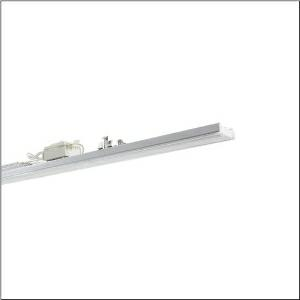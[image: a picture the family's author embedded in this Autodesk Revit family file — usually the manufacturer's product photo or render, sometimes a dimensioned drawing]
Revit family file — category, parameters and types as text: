
# Revit family: licross_21_recessed_ho_52te12dn4fxm3s
name_source: partatom
category: Lighting Fixtures
units: mm (PartAtom-declared; Revit-internal decimal feet)

## family parameters
Cut with Voids When Loaded = No
Host = Face
Light Source = No
Part Type = Normal
Room Calculation Point = No
Round Connector Dimension = Use Diameter
Shared = No

## types (1)
- --- (1 x LED, 930 lm, 7.5 W, 4000K)
    Apparent Load = 8 VA
    CIE Flux Codes = 69 91 98 100 100
    Color Rendering = 80
    Color Temperature = 4000K
    Default Elevation = 1800 mm
    Description = Licross 21 Recessed HO, luminaire insert, of sheet steel, galvanised, coil coated, white, length: 1.500mm, width: 66mm, height: 67mm, LED rated luminous flux: 15.000lm, light colour: 840, SDCM (Standard Deviation of Colour Matching)MacAdam ≤ 3 SDCM (initial), control gear: DALI 2 (for two DALI lines), with plug, 6-pole, with phase selection, for trunking rail, 14-core, mains connection: 220..240V, AC, 50/60Hz, rated input power: 88W, internal wiring halogen-free, for emergency light function, for trunking rail, 14-core, converter,control gear: single battery element, battery: LiFePO4, 9Ah, primary optical cover: cover, of PMMA, light emission: direct distribution, primary light characteristic: symmetric, protection rating (complete): IP54, insulation class (complete): insulation class I (protective earthing), certification: CE, UKCA, protection symbol: D if used in an environment with non-conductive dust loads with corresponding accessories, impact resistance: IK06, permissible ambient temperature for indoor applications: +5..+30°C, standard: EN 60598-2-22, LABS conformity tested according to VDMA 24364:2018-05, reducing of maximum allowable ambient temperature of 5°C with ceiling mounting, corresponds to IFS (International Featured Standards) requirements for safety and quality in the food industry, The light source and the operating device comply with the requirements of the Ecodesign Regulation (EU) 2019/2020 and are replaceable in accordance with this regulation, packaging unit: 1 piece
    Height = 58 mm
    Lamp = 1 x LED
    Lamp Light Flux = 930 lm
    Lamp Power = 7.5 W
    Lamp count = 1
    Length = 1500 mm
    Luminous efficacy = 124 lm/W
    Manufacturer = Siteco
    ModVariant = No
    Model = 52TE12DN4FXM3S
    Mounting Place = Ceiling
    Mounting Type = Pendant
    Number of Poles = 1
    OnlyDefault = Yes
    Power Factor = 1
    Product Name = Licross 21 Recessed HO
    Product group = luminaire insert | ceiling pendant
    ProductGroupID = 901
    Protection Class = Protection class I
    Protection Degree = IP 54
    RLX_Detail_Level = 1
    RLX_Emergency_Light_Flux = 0 lm
    RLX_Emergency_Type = 0
    RLX_Emergency_Type_DB = No
    RlxData = <blob elided: 25469 chars, md5=3e7f341c>
    Socket = socket
    Standby Power = 0 W
    System Light Flux = 930 lm
    System Power = 8 W
    Type Comments = : emergency light operation: 3 h
    Type Image = l_1296930.jpg
    URL = http://relux.com
    VarID = @adj_109225
    Voltage = 0 V
    Weight = 0.00 kg
    Width = 66 mm

## geometry (parser evidence)
native form markers: Blend x4, Sweep x11
no freeform markers — native parametric forms only
